# Revit family: MyFlowLounge
name_source: partatom
category: Furniture
units: mm (PartAtom-declared; Revit-internal decimal feet)

## family parameters
Always vertical = Yes
Cut with Voids When Loaded = No
OmniClass Number = 23.40.20.00
OmniClass Title = General Furniture and Specialties
Room Calculation Point = No
Shared = No
Work Plane-Based = No

## types (3) — shared parameters
BackrestInColour = Fabric (Light Grey)
BackrestOutColour = Fabric (Grey)
ManufactureURL = https://www.isku.com
Manufacturer = ISKU
SeatHeight = 450 mm  [stored 1.47638 ft]
zero-valued in all types: NorminalDepth, NorminalHeight

## per-type parameters (varying)
| type | Depth | Height | LoungeL | LoungeM | LoungeXL | Model | Width |
| MyFlow Lounge XL | 750 mm  [stored 2.46063 ft] | 1310 mm  [stored 4.2979 ft] | No | No | Yes | MyFlow Lounge - size XL | 970 mm |
| MyFlow Lounge L | 680 mm | 850 mm  [stored 2.78871 ft] | Yes | No | No | MyFlow Lounge - size L | 910 mm |
| MyFlow Lounge M | 590 mm | 750 mm  [stored 2.46063 ft] | No | Yes | No | MyFlow Lounge - size M | 630 mm  [stored 2.06693 ft] |

note: [stored X ft] marks values corroborated as IEEE doubles in the binary element streams (Revit-internal decimal feet)

## geometry (parser evidence)
native form markers: Sweep x32
no freeform markers — native parametric forms only
